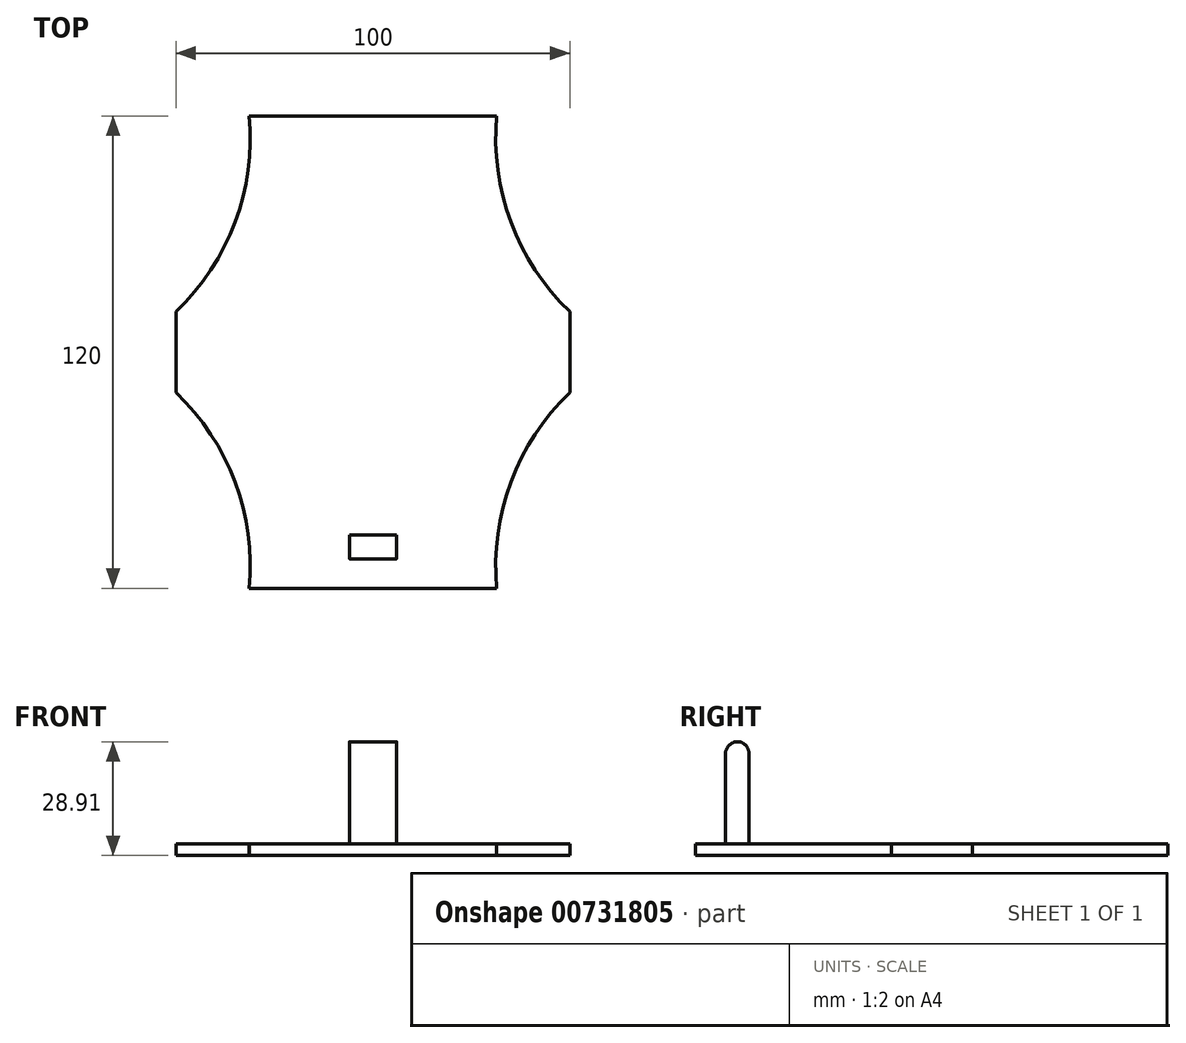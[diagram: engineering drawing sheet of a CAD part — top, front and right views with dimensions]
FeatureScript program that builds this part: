
annotation { "Feature Type Name" : "Feature", "Feature Type Description" : "" }
export const myFeature = defineFeature(function(context is Context, id is Id, definition is map)
    precondition{}
    {
        {
            var Q0;
            Q0=qCreatedBy(makeId("Top.planeOp"),FACE);
            var sketch = newSketch(context, id + "F0", { "sketchPlane" : qUnion([Q0])});
            skLineSegment(sketch, "E0.bottom", {"start": v(-55.08, 42.23) * mm, "end": v(-5.08, 42.23) * mm});
            skLineSegment(sketch, "E0.top", {"start": v(-55.08, -17.77) * mm, "end": v(-5.08, -17.77) * mm});
            skLineSegment(sketch, "E0.left", {"start": v(-55.08, 42.23) * mm, "end": v(-55.08, -17.77) * mm});
            skLineSegment(sketch, "E0.right", {"start": v(-5.08, 42.23) * mm, "end": v(-5.08, -17.77) * mm});
            skCircle(sketch, "E1", {"center": v(-97.5, 36.68) * mm, "radius": 61.26 * mm});
            skSolve(sketch);
        }
        {
            var Q0;
            {var subQ0=sQuery(id+"F0.wireOp",EDGE,"E0.left");var subQ1=sQuery(id+"F0.wireOp",EDGE,"E0.bottom");var subQ2=makeQuery(id+"F0.imprint","INTERSECT",VERTEX,{"derivedFrom":[subQ1,subQ0]});Q0=makeQuery(id+"F0.imprint","IMPRINT",FACE,{"disambiguationData":[TD([[makeQuery(id+"F0.imprint","IMPRINT",EDGE,{"disambiguationData":[TD([[subQ2,-1.0]])],"derivedFrom":subQ1}),1.0]])]});}
            var Q1;
            {var subQ0=sQuery(id+"F0.wireOp",EDGE,"E0.left");var subQ1=sQuery(id+"F0.wireOp",EDGE,"E0.bottom");var subQ2=makeQuery(id+"F0.imprint","INTERSECT",VERTEX,{"derivedFrom":[subQ1,subQ0]});Q1=makeQuery(id+"F0.imprint","IMPRINT",FACE,{"disambiguationData":[TD([[makeQuery(id+"F0.imprint","IMPRINT",EDGE,{"disambiguationData":[TD([[subQ2,-1.0]])],"derivedFrom":subQ1}),-1.0]])]});}
            var Q2;
            {var subQ2=sQuery(id+"F0.wireOp",EDGE,"E0.top");Q2=makeQuery(id+"F0.imprint","IMPRINT",FACE,{"disambiguationData":[TD([[makeQuery(id+"F0.imprint","IMPRINT",EDGE,{"derivedFrom":subQ2}),1.0]])]});}
            extrude(context, id + "F1", {"entities" : qUnion([Q0, Q1, Q2]), "depth" : 3 * mm, "offsetDistance" : 25 * mm});
        }
        {
            var Q0;
            {var subQ0=sQuery(id+"F0.wireOp",EDGE,"E0.left");var subQ1=sQuery(id+"F0.wireOp",EDGE,"E0.bottom");var subQ2=makeQuery(id+"F0.imprint","INTERSECT",VERTEX,{"derivedFrom":[subQ1,subQ0]});Q0=makeQuery(id+"F0.imprint","IMPRINT",FACE,{"disambiguationData":[TD([[makeQuery(id+"F0.imprint","IMPRINT",EDGE,{"disambiguationData":[TD([[subQ2,-1.0]])],"derivedFrom":subQ1}),-1.0]])]});}
            var Q1;
            {var subQ0=sQuery(id+"F0.wireOp",EDGE,"E0.left");var subQ1=sQuery(id+"F0.wireOp",EDGE,"E0.bottom");var subQ2=makeQuery(id+"F0.imprint","INTERSECT",VERTEX,{"derivedFrom":[subQ1,subQ0]});Q1=makeQuery(id+"F0.imprint","IMPRINT",FACE,{"disambiguationData":[TD([[makeQuery(id+"F0.imprint","IMPRINT",EDGE,{"disambiguationData":[TD([[subQ2,-1.0]])],"derivedFrom":subQ1}),1.0]])]});}
            extrude(context, id + "F2", {"entities" : qUnion([Q0, Q1]), "operationType" : NewBodyOperationType.REMOVE, "depth" : 57 * mm, "offsetDistance" : 25 * mm});
        }
        {
            var Q0;
            Q0=makeQuery(id+"F1.opExtrude","SWEPT_BODY",BODY,{"disambiguationData":[OSD([sQuery(id+"F0.wireOp",EDGE,"E0.bottom"),sQuery(id+"F0.wireOp",EDGE,"E0.top"),sQuery(id+"F0.wireOp",EDGE,"E0.left"),sQuery(id+"F0.wireOp",EDGE,"E0.right"),sQuery(id+"F0.wireOp",EDGE,"E1")])]});
            var Q1;
            Q1=makeQuery(id+"F1.opExtrude","SWEPT_FACE",FACE,{"disambiguationData":[OSD([sQuery(id+"F0.wireOp",EDGE,"E0.right")])]});
            mirror(context, id + "F3", {"operationType" : NewBodyOperationType.ADD, "entities" : qUnion([Q0]), "mirrorPlane" : qUnion([Q1])});
        }
        {
            var Q0;
            Q0=makeQuery(id+"F1.opExtrude","SWEPT_BODY",BODY,{"disambiguationData":[OSD([sQuery(id+"F0.wireOp",EDGE,"E0.bottom"),sQuery(id+"F0.wireOp",EDGE,"E0.top"),sQuery(id+"F0.wireOp",EDGE,"E0.left"),sQuery(id+"F0.wireOp",EDGE,"E0.right"),sQuery(id+"F0.wireOp",EDGE,"E1")])]});
            var Q1;
            {var subQ0=makeQuery(id+"F1.opExtrude","SWEPT_FACE",FACE,{"disambiguationData":[OSD([sQuery(id+"F0.wireOp",EDGE,"E0.top")])]});Q1=makeQuery(id+"F3.boolean.opBoolean","MERGE",FACE,{"derivedFrom":[subQ0,makeQuery(id+"F3.opPattern","COPY",FACE,{"derivedFrom":subQ0,"instanceName":"1"})]});}
            mirror(context, id + "F4", {"operationType" : NewBodyOperationType.ADD, "entities" : qUnion([Q0]), "mirrorPlane" : qUnion([Q1])});
        }
        {
            var Q0;
            {var subQ0=makeQuery(id+"F1.opExtrude","CAP_FACE",FACE,{"disambiguationData":[OSD([sQuery(id+"F0.wireOp",EDGE,"E0.bottom"),sQuery(id+"F0.wireOp",EDGE,"E0.top"),sQuery(id+"F0.wireOp",EDGE,"E0.left"),sQuery(id+"F0.wireOp",EDGE,"E0.right"),sQuery(id+"F0.wireOp",EDGE,"E1")])],"isStart":false});var subQ1=makeQuery(id+"F3.boolean.opBoolean","MERGE",FACE,{"derivedFrom":[subQ0,makeQuery(id+"F3.opPattern","COPY",FACE,{"derivedFrom":subQ0,"instanceName":"1"})]});Q0=makeQuery(id+"F4.boolean.opBoolean","MERGE",FACE,{"derivedFrom":[subQ1,makeQuery(id+"F4.opPattern","COPY",FACE,{"derivedFrom":subQ1,"instanceName":"1"})]});}
            var sketch = newSketch(context, id + "F5", { "sketchPlane" : qUnion([Q0])});
            skLineSegment(sketch, "E2", {"start": v(-36.5, -77.77) * mm, "end": v(-5.08, -77.77) * mm});
            skLineSegment(sketch, "E3", {"start": v(-5.08, -77.77) * mm, "end": v(-5.08, -70.27) * mm});
            skLineSegment(sketch, "E4.bottom", {"start": v(-5.08, -64.27) * mm, "end": v(0.92, -64.27) * mm});
            skLineSegment(sketch, "E4.top", {"start": v(-5.08, -70.27) * mm, "end": v(0.92, -70.27) * mm});
            skLineSegment(sketch, "E4.right", {"start": v(0.92, -64.27) * mm, "end": v(0.92, -70.27) * mm});
            skLineSegment(sketch, "E5.bottom", {"start": v(-5.08, -64.27) * mm, "end": v(-11.08, -64.27) * mm});
            skLineSegment(sketch, "E5.top", {"start": v(-5.08, -70.27) * mm, "end": v(-11.08, -70.27) * mm});
            skLineSegment(sketch, "E5.right", {"start": v(-11.08, -64.27) * mm, "end": v(-11.08, -70.27) * mm});
            skLineSegment(sketch, "E6.trimOffspring", {"start": v(-5.08, -64.27) * mm, "end": v(-5.08, 64.54) * mm});
            skSolve(sketch);
        }
        {
            var Q0;
            Q0=makeQuery(id+"F5.imprint","IMPRINT",FACE,{"disambiguationData":[TD([[makeQuery(id+"F5.imprint","IMPRINT",EDGE,{"derivedFrom":sQuery(id+"F5.wireOp",EDGE,"E4.bottom")}),-1.0]])]});
            extrude(context, id + "F6", {"entities" : qUnion([Q0]), "operationType" : NewBodyOperationType.ADD, "depth" : 26 * mm, "offsetDistance" : 25 * mm});
        }
        {
            var Q0;
            Q0=makeQuery(id+"F6.opExtrude","CAP_EDGE",EDGE,{"disambiguationData":[OSD([sQuery(id+"F5.wireOp",EDGE,"E4.top"),sQuery(id+"F5.wireOp",EDGE,"E5.top")])],"isStart":false});
            fillet(context, id + "F7", {"entities" : qUnion([Q0]), "radius" : 3.38 * mm, "tangentPropagation" : true, "allowEdgeOverflow" : false});
        }
        {
            var Q0;
            Q0=makeQuery(id+"F6.opExtrude","CAP_EDGE",EDGE,{"disambiguationData":[OSD([sQuery(id+"F5.wireOp",EDGE,"E4.bottom"),sQuery(id+"F5.wireOp",EDGE,"E5.bottom")])],"isStart":false});
            fillet(context, id + "F8", {"entities" : qUnion([Q0]), "radius" : 2.9 * mm, "tangentPropagation" : true, "allowEdgeOverflow" : false});
        }
    });
